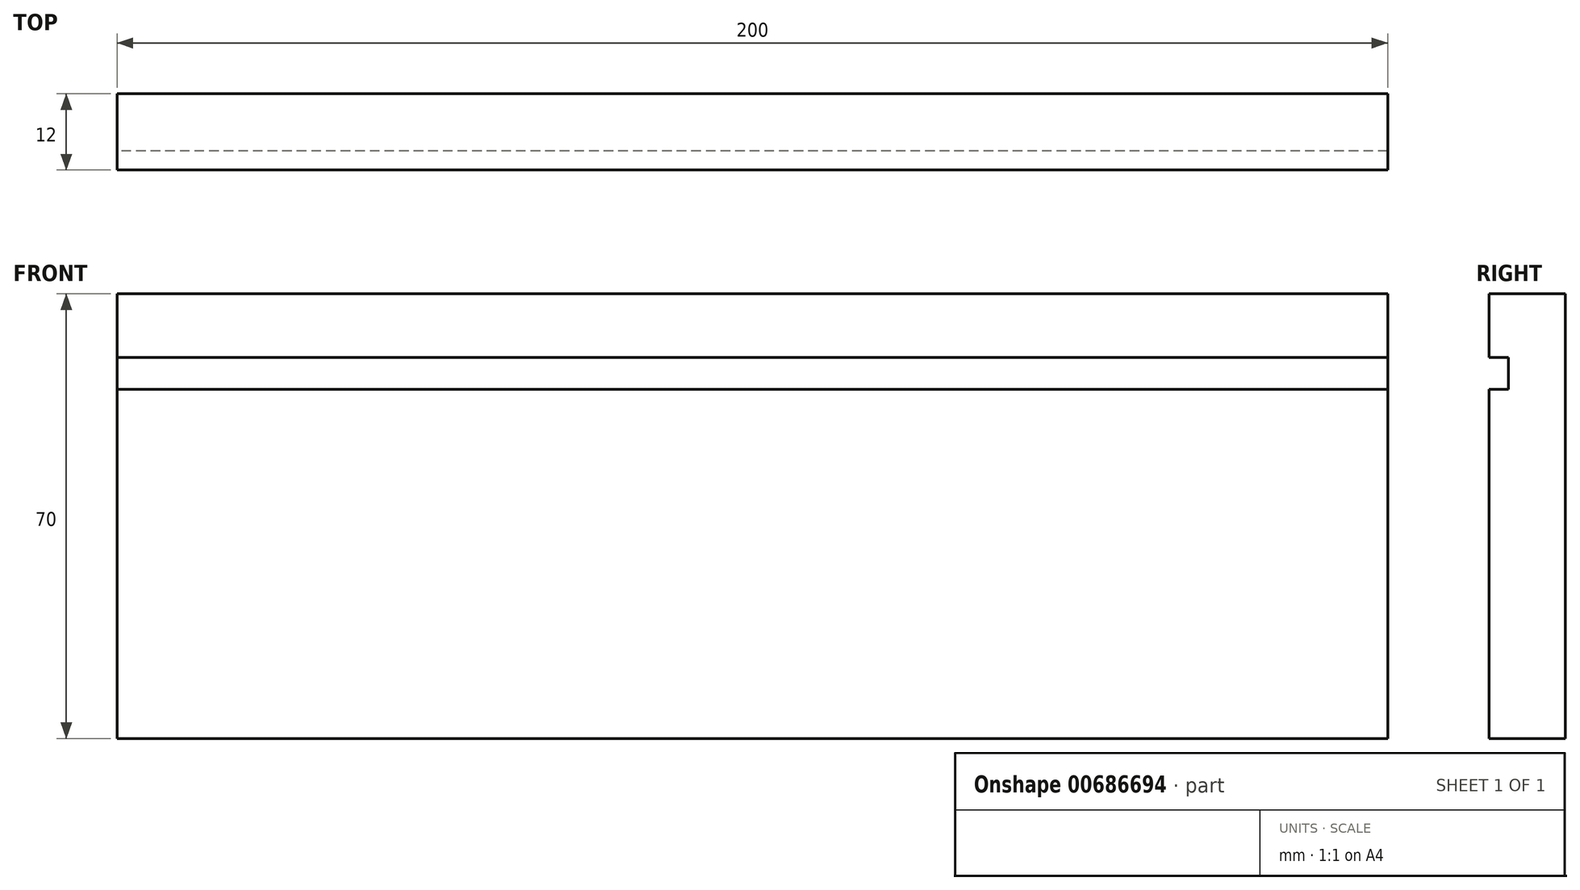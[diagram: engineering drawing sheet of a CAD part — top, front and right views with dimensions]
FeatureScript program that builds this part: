
annotation { "Feature Type Name" : "Feature", "Feature Type Description" : "" }
export const myFeature = defineFeature(function(context is Context, id is Id, definition is map)
    precondition{}
    {
        {
            var Q0;
            Q0=qCreatedBy(makeId("Right.planeOp"),FACE);
            var sketch = newSketch(context, id + "F0", { "sketchPlane" : qUnion([Q0])});
            skLineSegment(sketch, "E0.bottom", {"start": v(0, 0) * mm, "end": v(12, 0) * mm});
            skLineSegment(sketch, "E0.top", {"start": v(0, 70) * mm, "end": v(12, 70) * mm});
            skLineSegment(sketch, "E0.left", {"start": v(0, 0) * mm, "end": v(0, 55) * mm});
            skLineSegment(sketch, "E0.right", {"start": v(12, 0) * mm, "end": v(12, 70) * mm});
            skLineSegment(sketch, "E1.bottom", {"start": v(0, 60) * mm, "end": v(3, 60) * mm});
            skLineSegment(sketch, "E1.top", {"start": v(0, 55) * mm, "end": v(3, 55) * mm});
            skLineSegment(sketch, "E1.right", {"start": v(3, 60) * mm, "end": v(3, 55) * mm});
            skLineSegment(sketch, "E2.trimOffspring", {"start": v(0, 60) * mm, "end": v(0, 70) * mm});
            skSolve(sketch);
        }
        {
            var Q0;
            Q0=qSketchRegion(id+"F0",true);
            extrude(context, id + "F1", {"entities" : qUnion([Q0]), "depth" : 200 * mm, "offsetDistance" : 25 * mm});
        }
    });
